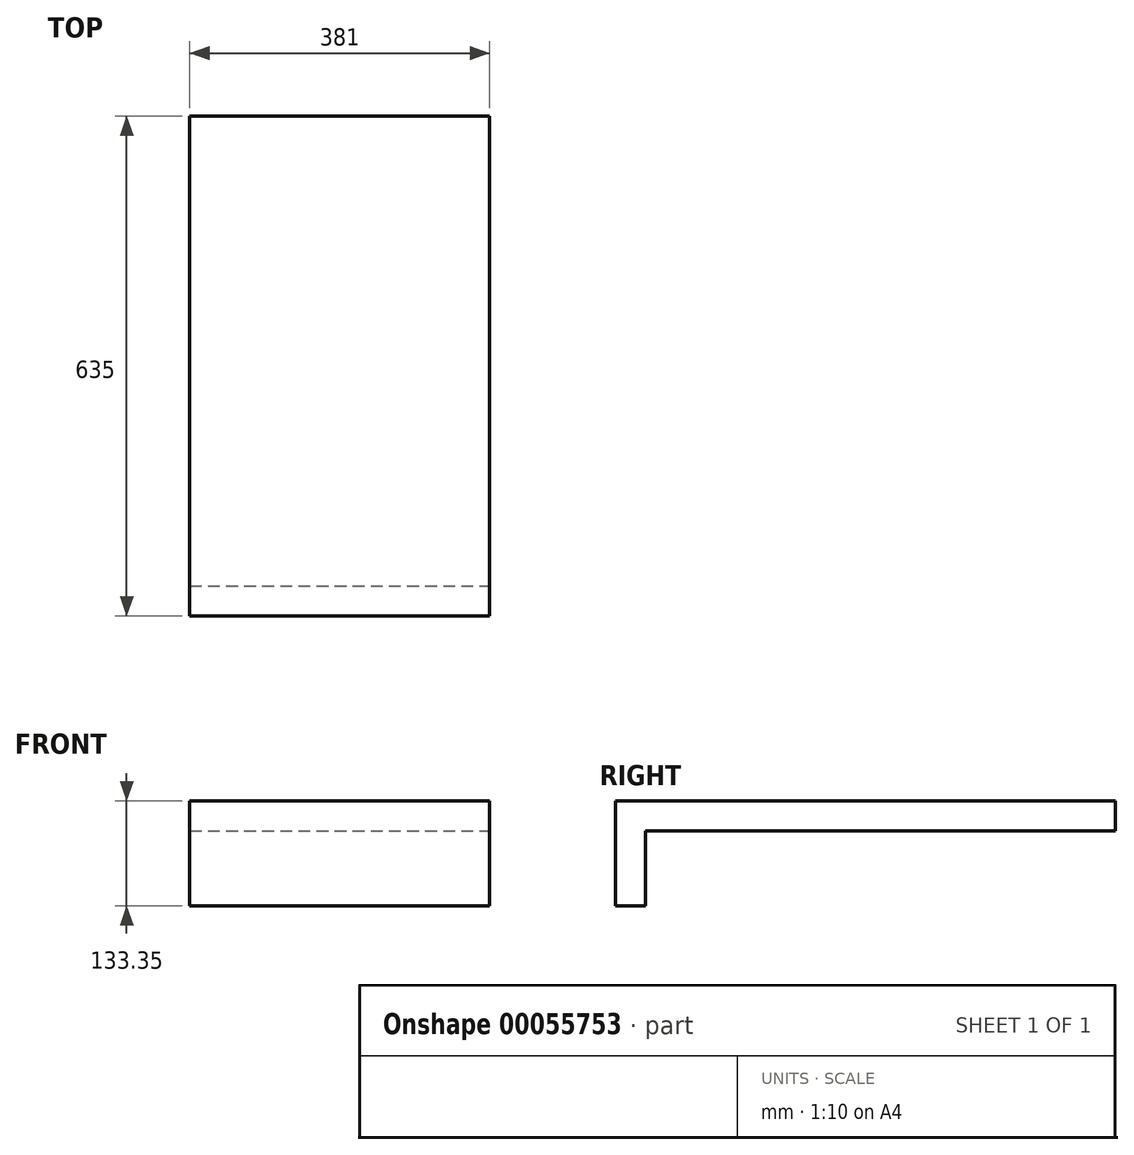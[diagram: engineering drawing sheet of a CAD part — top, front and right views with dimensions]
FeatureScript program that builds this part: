
annotation { "Feature Type Name" : "Feature", "Feature Type Description" : "" }
export const myFeature = defineFeature(function(context is Context, id is Id, definition is map)
    precondition{}
    {
        {
            var Q0;
            Q0=qCreatedBy(makeId("Top.planeOp"),FACE);
            var sketch = newSketch(context, id + "F0", { "sketchPlane" : qUnion([Q0])});
            skLineSegment(sketch, "E0.rect.bottom", {"start": v(190.5, 317.5) * mm, "end": v(-190.5, 317.5) * mm});
            skLineSegment(sketch, "E0.rect.top", {"start": v(190.5, -317.5) * mm, "end": v(-190.5, -317.5) * mm});
            skLineSegment(sketch, "E0.rect.left", {"start": v(190.5, 317.5) * mm, "end": v(190.5, -317.5) * mm});
            skLineSegment(sketch, "E0.rect.right", {"start": v(-190.5, 317.5) * mm, "end": v(-190.5, -317.5) * mm});
            skPoint(sketch, "E0.rect.middle", {"position": v(0, 0) * mm});
            skSolve(sketch);
        }
        {
            var Q0;
            Q0=makeQuery(id+"F0.imprint","IMPRINT",FACE,{"disambiguationData":[TD([[makeQuery(id+"F0.imprint","IMPRINT",EDGE,{"derivedFrom":sQuery(id+"F0.wireOp",EDGE,"E0.rect.bottom")}),1.0]])]});
            extrude(context, id + "F1", {"entities" : qUnion([Q0]), "depth" : 38.1 * mm});
        }
        {
            var Q0;
            Q0=makeQuery(id+"F1.opExtrude","CAP_FACE",FACE,{"disambiguationData":[OSD([sQuery(id+"F0.wireOp",EDGE,"E0.rect.bottom"),sQuery(id+"F0.wireOp",EDGE,"E0.rect.top"),sQuery(id+"F0.wireOp",EDGE,"E0.rect.left"),sQuery(id+"F0.wireOp",EDGE,"E0.rect.right")])],"isStart":true});
            var sketch = newSketch(context, id + "F2", { "sketchPlane" : qUnion([Q0])});
            skLineSegment(sketch, "E1.bottom", {"start": v(-190.5, 317.5) * mm, "end": v(190.5, 317.5) * mm});
            skLineSegment(sketch, "E1.top", {"start": v(-190.5, 279.4) * mm, "end": v(190.5, 279.4) * mm});
            skLineSegment(sketch, "E1.left", {"start": v(-190.5, 317.5) * mm, "end": v(-190.5, 279.4) * mm});
            skLineSegment(sketch, "E1.right", {"start": v(190.5, 317.5) * mm, "end": v(190.5, 279.4) * mm});
            skSolve(sketch);
        }
        {
            var Q0;
            Q0=qSketchRegion(id+"F2",true);
            extrude(context, id + "F3", {"entities" : qUnion([Q0]), "operationType" : NewBodyOperationType.ADD, "depth" : 95.25 * mm});
        }
    });
